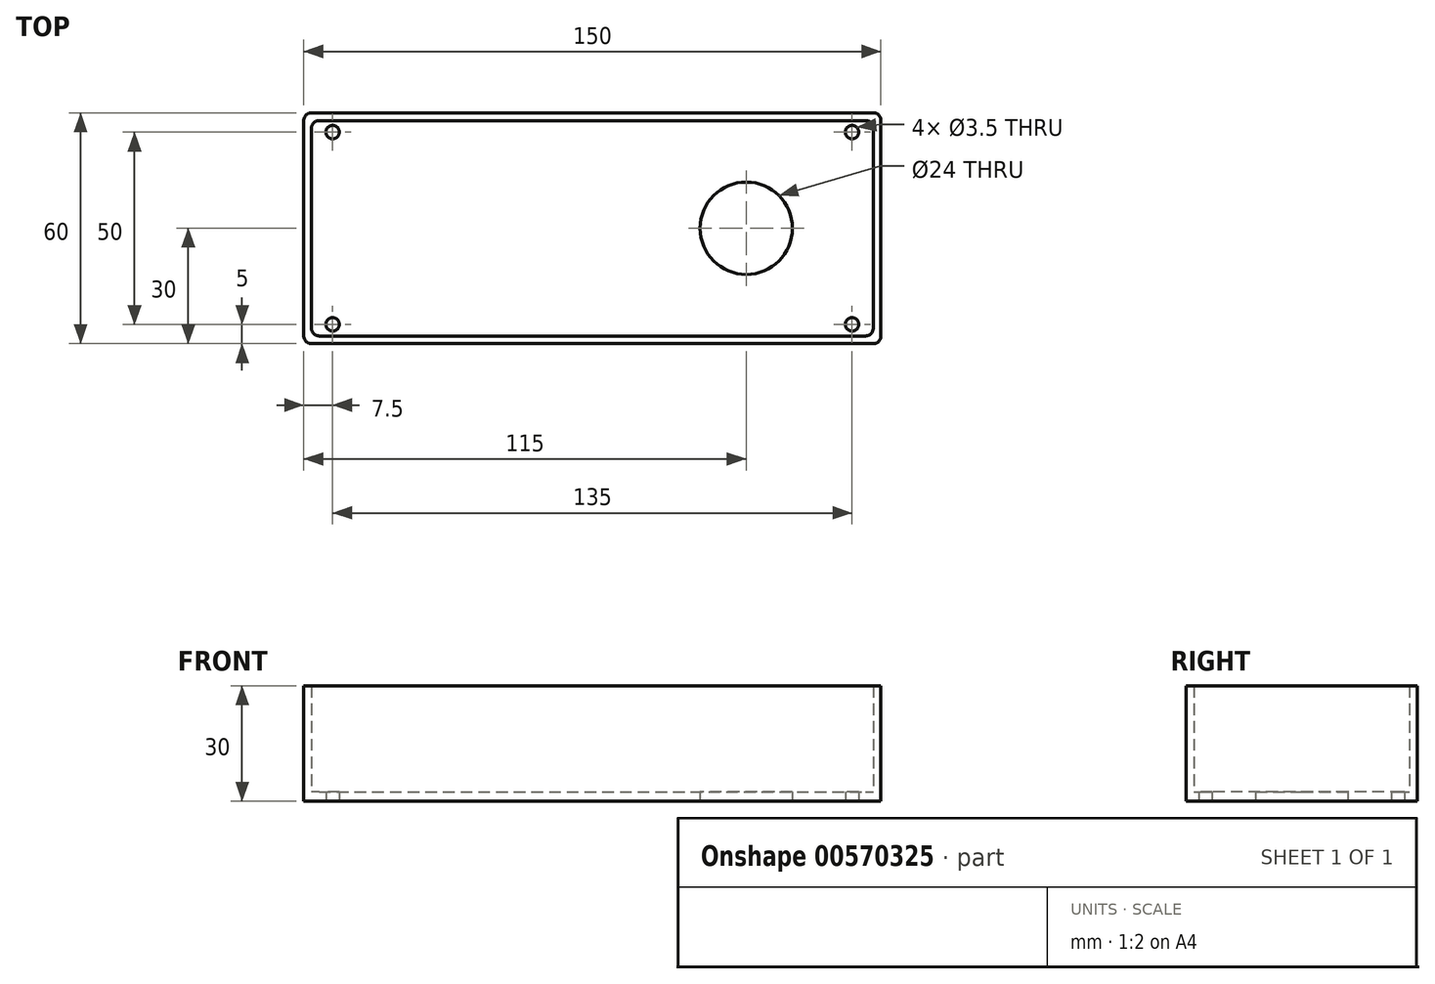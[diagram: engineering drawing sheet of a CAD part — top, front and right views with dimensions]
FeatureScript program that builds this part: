
annotation { "Feature Type Name" : "Feature", "Feature Type Description" : "" }
export const myFeature = defineFeature(function(context is Context, id is Id, definition is map)
    precondition{}
    {
        {
            var Q0;
            Q0=qCreatedBy(makeId("Top.planeOp"),FACE);
            var sketch = newSketch(context, id + "F0", { "sketchPlane" : qUnion([Q0])});
            skLineSegment(sketch, "E0.bottom", {"start": v(75, -30) * mm, "end": v(-75, -30) * mm});
            skLineSegment(sketch, "E0.top", {"start": v(75, 30) * mm, "end": v(-75, 30) * mm});
            skLineSegment(sketch, "E0.left", {"start": v(75, -30) * mm, "end": v(75, 30) * mm});
            skLineSegment(sketch, "E0.right", {"start": v(-75, -30) * mm, "end": v(-75, 30) * mm});
            skPoint(sketch, "E0.middle", {"position": v(0, 0) * mm});
            skLineSegment(sketch, "E1", {"start": v(0, 0) * mm, "end": v(-67.5, 0) * mm});
            skPoint(sketch, "E1.endSnap0", {"position": v(-75, 0) * mm});
            skLineSegment(sketch, "E2", {"start": v(-67.5, 0) * mm, "end": v(-67.5, -25) * mm});
            skLineSegment(sketch, "E3", {"start": v(-67.5, 0) * mm, "end": v(-67.5, 25) * mm});
            skCircle(sketch, "E4", {"center": v(-67.5, 25) * mm, "radius": 1.75 * mm});
            skCircle(sketch, "E5", {"center": v(-67.5, -25) * mm, "radius": 1.75 * mm});
            skLineSegment(sketch, "E6", {"start": v(0, 0) * mm, "end": v(67.5, 0) * mm});
            skLineSegment(sketch, "E7", {"start": v(67.5, 0) * mm, "end": v(67.5, 25) * mm});
            skLineSegment(sketch, "E8", {"start": v(67.5, 0) * mm, "end": v(67.5, -25) * mm});
            skCircle(sketch, "E9", {"center": v(67.5, 25) * mm, "radius": 1.75 * mm});
            skCircle(sketch, "E10", {"center": v(67.5, -25) * mm, "radius": 1.75 * mm});
            skLineSegment(sketch, "E11", {"start": v(0, 0) * mm, "end": v(40, 0) * mm});
            skCircle(sketch, "E12", {"center": v(40, 0) * mm, "radius": 12 * mm});
            skSolve(sketch);
        }
        {
            var Q0;
            Q0 = qSketchRegion(id + "F0", true);
            extrude(context, id + "F1", {"entities" : qUnion([Q0]), "depth" : 2.5 * mm, "offsetDistance" : 25 * mm});
        }
        {
            var Q0;
            Q0=qCreatedBy(makeId("Top.planeOp"),FACE);
            var sketch = newSketch(context, id + "F2", { "sketchPlane" : qUnion([Q0])});
            skLineSegment(sketch, "E13.bottom", {"start": v(75, -30) * mm, "end": v(-75, -30) * mm});
            skLineSegment(sketch, "E13.top", {"start": v(75, 30) * mm, "end": v(-75, 30) * mm});
            skLineSegment(sketch, "E13.left", {"start": v(75, -30) * mm, "end": v(75, 30) * mm});
            skLineSegment(sketch, "E13.right", {"start": v(-75, -30) * mm, "end": v(-75, 30) * mm});
            skPoint(sketch, "E13.middle", {"position": v(0, 0) * mm});
            skLineSegment(sketch, "E14.bottom", {"start": v(73, -28) * mm, "end": v(-73, -28) * mm});
            skLineSegment(sketch, "E14.top", {"start": v(73, 28) * mm, "end": v(-73, 28) * mm});
            skLineSegment(sketch, "E14.left", {"start": v(73, -28) * mm, "end": v(73, 28) * mm});
            skLineSegment(sketch, "E14.right", {"start": v(-73, -28) * mm, "end": v(-73, 28) * mm});
            skSolve(sketch);
        }
        {
            var Q0;
            Q0 = qSketchRegion(id + "F2", true);
            extrude(context, id + "F3", {"entities" : qUnion([Q0]), "operationType" : NewBodyOperationType.ADD, "depth" : 30 * mm, "offsetDistance" : 25 * mm});
        }
        {
            var Q0;
            Q0=makeQuery(id+"F3.opExtrude","SWEPT_EDGE",EDGE,{"disambiguationData":[OSD([sQuery(id+"F2.wireOp",EDGE,"E14.top"),sQuery(id+"F2.wireOp",EDGE,"E14.right")])]});
            var Q1;
            Q1=makeQuery(id+"F3.opExtrude","SWEPT_EDGE",EDGE,{"disambiguationData":[OSD([sQuery(id+"F2.wireOp",EDGE,"E14.top"),sQuery(id+"F2.wireOp",EDGE,"E14.left")])]});
            var Q2;
            Q2=makeQuery(id+"F3.opExtrude","SWEPT_EDGE",EDGE,{"disambiguationData":[OSD([sQuery(id+"F2.wireOp",EDGE,"E14.bottom"),sQuery(id+"F2.wireOp",EDGE,"E14.right")])]});
            var Q3;
            Q3=makeQuery(id+"F3.opExtrude","SWEPT_EDGE",EDGE,{"disambiguationData":[OSD([sQuery(id+"F2.wireOp",EDGE,"E14.bottom"),sQuery(id+"F2.wireOp",EDGE,"E14.left")])]});
            var Q4;
            Q4=makeQuery(id+"F3.boolean.opBoolean","MERGE",EDGE,{"derivedFrom":[makeQuery(id+"F1.opExtrude","SWEPT_EDGE",EDGE,{"disambiguationData":[OSD([sQuery(id+"F0.wireOp",EDGE,"E0.top"),sQuery(id+"F0.wireOp",EDGE,"E0.right")])]}),makeQuery(id+"F3.opExtrude","SWEPT_EDGE",EDGE,{"disambiguationData":[OSD([sQuery(id+"F2.wireOp",EDGE,"E13.top"),sQuery(id+"F2.wireOp",EDGE,"E13.right")])]})]});
            var Q5;
            Q5=makeQuery(id+"F3.boolean.opBoolean","MERGE",EDGE,{"derivedFrom":[makeQuery(id+"F1.opExtrude","SWEPT_EDGE",EDGE,{"disambiguationData":[OSD([sQuery(id+"F0.wireOp",EDGE,"E0.bottom"),sQuery(id+"F0.wireOp",EDGE,"E0.right")])]}),makeQuery(id+"F3.opExtrude","SWEPT_EDGE",EDGE,{"disambiguationData":[OSD([sQuery(id+"F2.wireOp",EDGE,"E13.bottom"),sQuery(id+"F2.wireOp",EDGE,"E13.right")])]})]});
            var Q6;
            Q6=makeQuery(id+"F3.boolean.opBoolean","MERGE",EDGE,{"derivedFrom":[makeQuery(id+"F1.opExtrude","SWEPT_EDGE",EDGE,{"disambiguationData":[OSD([sQuery(id+"F0.wireOp",EDGE,"E0.bottom"),sQuery(id+"F0.wireOp",EDGE,"E0.left")])]}),makeQuery(id+"F3.opExtrude","SWEPT_EDGE",EDGE,{"disambiguationData":[OSD([sQuery(id+"F2.wireOp",EDGE,"E13.bottom"),sQuery(id+"F2.wireOp",EDGE,"E13.left")])]})]});
            var Q7;
            Q7=makeQuery(id+"F3.boolean.opBoolean","MERGE",EDGE,{"derivedFrom":[makeQuery(id+"F1.opExtrude","SWEPT_EDGE",EDGE,{"disambiguationData":[OSD([sQuery(id+"F0.wireOp",EDGE,"E0.top"),sQuery(id+"F0.wireOp",EDGE,"E0.left")])]}),makeQuery(id+"F3.opExtrude","SWEPT_EDGE",EDGE,{"disambiguationData":[OSD([sQuery(id+"F2.wireOp",EDGE,"E13.top"),sQuery(id+"F2.wireOp",EDGE,"E13.left")])]})]});
            fillet(context, id + "F4", {"entities" : qUnion([Q0, Q1, Q2, Q3, Q4, Q5, Q6, Q7]), "radius" : 2 * mm, "tangentPropagation" : true, "allowEdgeOverflow" : false});
        }
    });
